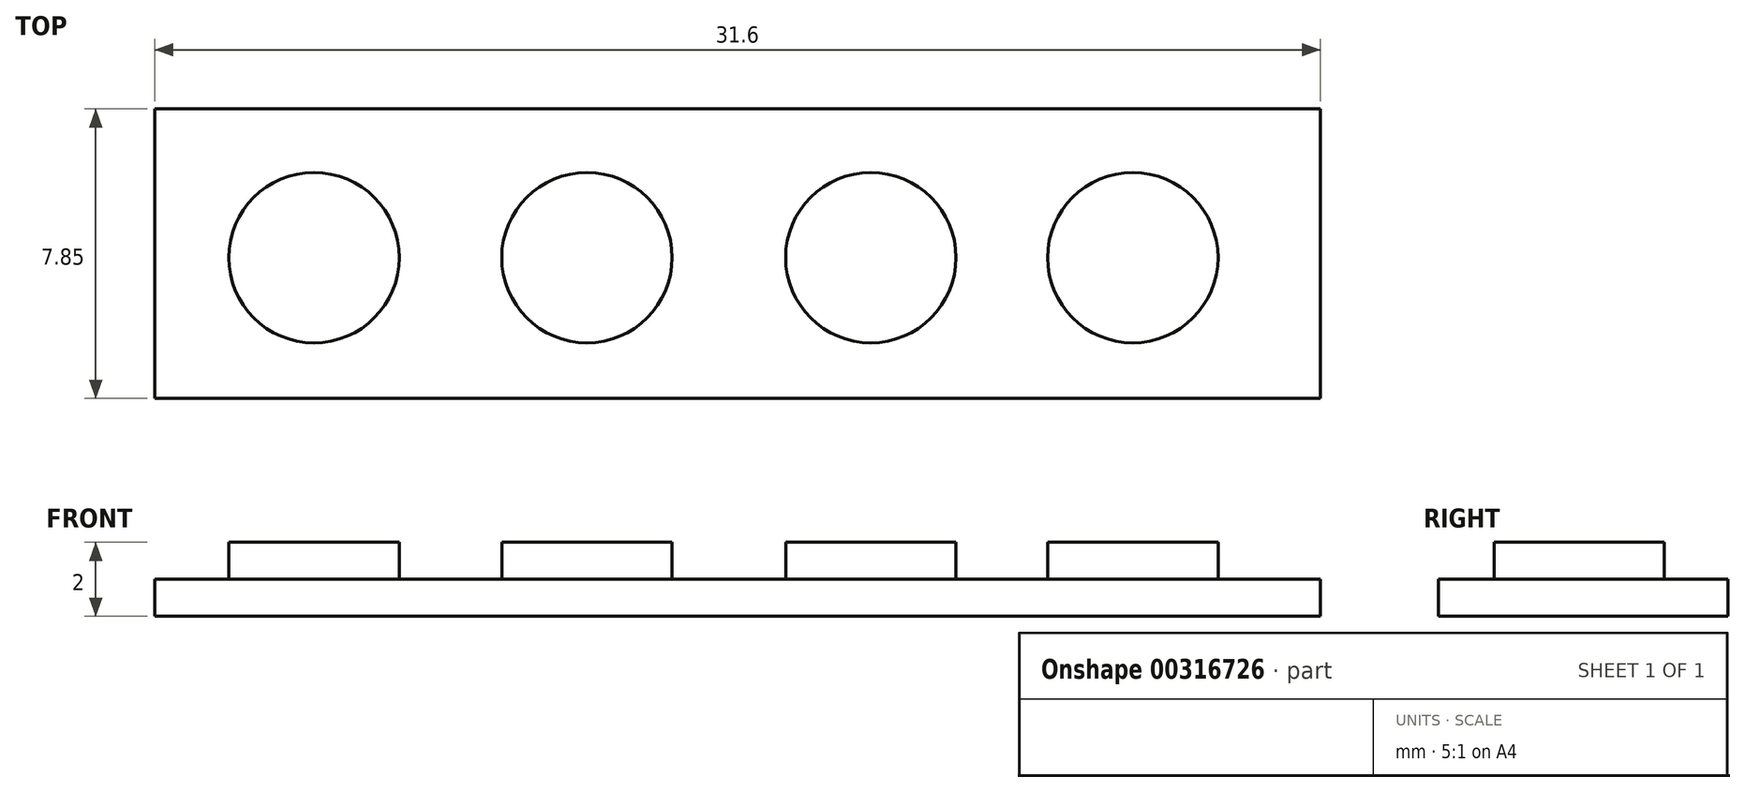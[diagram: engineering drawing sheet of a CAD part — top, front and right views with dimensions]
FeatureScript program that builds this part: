
annotation { "Feature Type Name" : "Feature", "Feature Type Description" : "" }
export const myFeature = defineFeature(function(context is Context, id is Id, definition is map)
    precondition{}
    {
        {
            var Q0;
            Q0=qCreatedBy(makeId("Top.planeOp"),FACE);
            var sketch = newSketch(context, id + "F0", { "sketchPlane" : qUnion([Q0])});
            skLineSegment(sketch, "E0.bottom", {"start": v(-12.62, -1.58) * mm, "end": v(18.98, -1.58) * mm});
            skLineSegment(sketch, "E0.top", {"start": v(-12.62, -9.43) * mm, "end": v(18.98, -9.43) * mm});
            skLineSegment(sketch, "E0.left", {"start": v(-12.62, -1.58) * mm, "end": v(-12.62, -9.43) * mm});
            skLineSegment(sketch, "E0.right", {"start": v(18.98, -1.58) * mm, "end": v(18.98, -9.43) * mm});
            skCircle(sketch, "E1", {"center": v(-8.3, -5.61) * mm, "radius": 2.31 * mm});
            skCircle(sketch, "E2", {"center": v(-0.9, -5.61) * mm, "radius": 2.31 * mm});
            skCircle(sketch, "E3", {"center": v(6.8, -5.61) * mm, "radius": 2.31 * mm});
            skCircle(sketch, "E4", {"center": v(13.9, -5.61) * mm, "radius": 2.31 * mm});
            skSolve(sketch);
        }
        {
            var Q0;
            Q0=makeQuery(id+"F0.imprint","IMPRINT",FACE,{"disambiguationData":[TD([[makeQuery(id+"F0.imprint","IMPRINT",EDGE,{"derivedFrom":sQuery(id+"F0.wireOp",EDGE,"E1")}),1.0]])]});
            var Q1;
            Q1=makeQuery(id+"F0.imprint","IMPRINT",FACE,{"disambiguationData":[TD([[makeQuery(id+"F0.imprint","IMPRINT",EDGE,{"derivedFrom":sQuery(id+"F0.wireOp",EDGE,"E2")}),1.0]])]});
            var Q2;
            Q2=makeQuery(id+"F0.imprint","IMPRINT",FACE,{"disambiguationData":[TD([[makeQuery(id+"F0.imprint","IMPRINT",EDGE,{"derivedFrom":sQuery(id+"F0.wireOp",EDGE,"E3")}),1.0]])]});
            var Q3;
            Q3=makeQuery(id+"F0.imprint","IMPRINT",FACE,{"disambiguationData":[TD([[makeQuery(id+"F0.imprint","IMPRINT",EDGE,{"derivedFrom":sQuery(id+"F0.wireOp",EDGE,"E4")}),1.0]])]});
            extrude(context, id + "F1", {"entities" : qUnion([Q0, Q1, Q2, Q3]), "depth" : 2 * mm});
        }
        {
            var Q0;
            Q0 = qSketchRegion(id + "F0", true);
            extrude(context, id + "F2", {"entities" : qUnion([Q0]), "operationType" : NewBodyOperationType.ADD, "depth" : 1 * mm});
        }
    });
